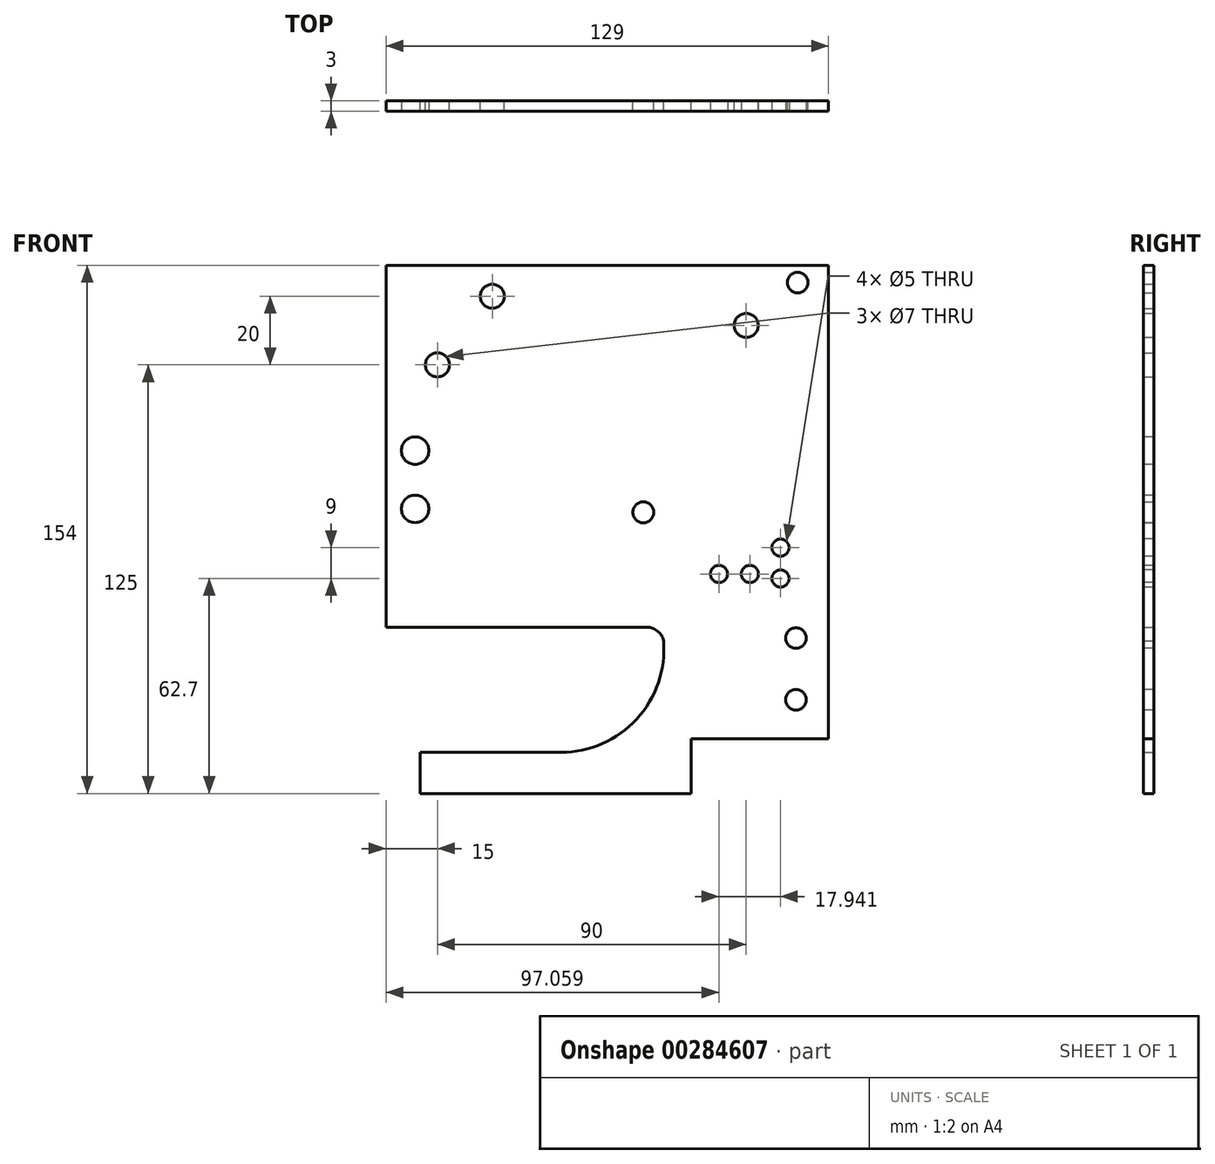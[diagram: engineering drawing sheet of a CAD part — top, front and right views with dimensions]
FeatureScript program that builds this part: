
annotation { "Feature Type Name" : "Feature", "Feature Type Description" : "" }
export const myFeature = defineFeature(function(context is Context, id is Id, definition is map)
    precondition{}
    {
        {
            var Q0;
            Q0=qCreatedBy(makeId("Front.planeOp"),FACE);
            var sketch = newSketch(context, id + "F0", { "sketchPlane" : qUnion([Q0])});
            skLineSegment(sketch, "E0", {"start": v(0, 0) * mm, "end": v(129, 0) * mm});
            skLineSegment(sketch, "E1", {"start": v(129, 0) * mm, "end": v(129, -138) * mm});
            skLineSegment(sketch, "E2", {"start": v(129, -138) * mm, "end": v(89, -138) * mm});
            skLineSegment(sketch, "E3", {"start": v(89, -138) * mm, "end": v(89, -154) * mm});
            skLineSegment(sketch, "E4", {"start": v(89, -154) * mm, "end": v(10, -154) * mm});
            skLineSegment(sketch, "E5", {"start": v(10, -154) * mm, "end": v(10, -142) * mm});
            skLineSegment(sketch, "E6", {"start": v(0, 0) * mm, "end": v(0, -105.5) * mm});
            skLineSegment(sketch, "E7", {"start": v(0, -105.5) * mm, "end": v(76, -105.5) * mm});
            skLineSegment(sketch, "E8", {"start": v(10, -142) * mm, "end": v(51, -142) * mm});
            skLineSegment(sketch, "E9", {"start": v(51, -142) * mm, "end": v(51, -112) * mm, "construction": true});
            skArc(sketch, "E10", {"start": v(51, -142) * mm, "mid": v(73.09, -132.3) * mm, "end": v(80.9, -109.47) * mm});
            skArc(sketch, "E11", {"start": v(80.9, -109.47) * mm, "mid": v(79.15, -106.62) * mm, "end": v(76, -105.5) * mm});
            skLineSegment(sketch, "E12", {"start": v(75, -154) * mm, "end": v(75, -127) * mm, "construction": true});
            skLineSegment(sketch, "E13", {"start": v(75, -127) * mm, "end": v(129, -127) * mm, "construction": true});
            skLineSegment(sketch, "E14", {"start": v(120, -138) * mm, "end": v(120, -99) * mm, "construction": true});
            skLineSegment(sketch, "E15", {"start": v(120, -99) * mm, "end": v(129, -99) * mm, "construction": true});
            skLineSegment(sketch, "E16", {"start": v(120, -99) * mm, "end": v(120, -5) * mm, "construction": true});
            skLineSegment(sketch, "E17", {"start": v(0, -9) * mm, "end": v(31, -9) * mm, "construction": true});
            skLineSegment(sketch, "E18", {"start": v(31, -9) * mm, "end": v(31, 0) * mm, "construction": true});
            skLineSegment(sketch, "E19", {"start": v(0, -29) * mm, "end": v(15, -29) * mm, "construction": true});
            skLineSegment(sketch, "E20", {"start": v(15, -29) * mm, "end": v(15, 0) * mm, "construction": true});
            skLineSegment(sketch, "E21", {"start": v(105, 0) * mm, "end": v(105, -17.5) * mm, "construction": true});
            skLineSegment(sketch, "E22", {"start": v(105, -17.5) * mm, "end": v(129, -17.5) * mm, "construction": true});
            skLineSegment(sketch, "E23", {"start": v(75, -127) * mm, "end": v(75, -72) * mm, "construction": true});
            skSolve(sketch);
        }
        {
            var Q0;
            Q0=qSketchRegion(id+"F0",true);
            extrude(context, id + "F1", {"entities" : qUnion([Q0]), "depth" : 3 * mm});
        }
        {
            var Q0;
            Q0=sQuery(id+"F0.wireOp",VERTEX,"E16.end");
            var Q1;
            Q1=makeQuery(id+"F1.opExtrude","SWEPT_BODY",BODY,{"disambiguationData":[OSD([sQuery(id+"F0.wireOp",EDGE,"E0"),sQuery(id+"F0.wireOp",EDGE,"E1"),sQuery(id+"F0.wireOp",EDGE,"E2"),sQuery(id+"F0.wireOp",EDGE,"E3"),sQuery(id+"F0.wireOp",EDGE,"E4"),sQuery(id+"F0.wireOp",EDGE,"E5"),sQuery(id+"F0.wireOp",EDGE,"E6"),sQuery(id+"F0.wireOp",EDGE,"E7"),sQuery(id+"F0.wireOp",EDGE,"E8"),sQuery(id+"F0.wireOp",EDGE,"E10"),sQuery(id+"F0.wireOp",EDGE,"E11")])]});
            hole(context, id + "F2", {"style" : HoleStyle.SIMPLE, "endStyle" : HoleEndStyle.THROUGH, "oppositeDirection" : true, "holeDiameter" : 6 * mm, "locations" : qUnion([Q0]), "scope" : qUnion([Q1]), "tappedDepth" : 12 * mm, "tapClearance" : 3});
        }
        {
            var Q0;
            Q0=sQuery(id+"F0.wireOp",VERTEX,"E19.end");
            var Q1;
            Q1=sQuery(id+"F0.wireOp",VERTEX,"E18.start");
            var Q2;
            Q2=sQuery(id+"F0.wireOp",VERTEX,"E21.end");
            var Q3;
            Q3=makeQuery(id+"F1.opExtrude","SWEPT_BODY",BODY,{"disambiguationData":[OSD([sQuery(id+"F0.wireOp",EDGE,"E0"),sQuery(id+"F0.wireOp",EDGE,"E1"),sQuery(id+"F0.wireOp",EDGE,"E2"),sQuery(id+"F0.wireOp",EDGE,"E3"),sQuery(id+"F0.wireOp",EDGE,"E4"),sQuery(id+"F0.wireOp",EDGE,"E5"),sQuery(id+"F0.wireOp",EDGE,"E6"),sQuery(id+"F0.wireOp",EDGE,"E7"),sQuery(id+"F0.wireOp",EDGE,"E8"),sQuery(id+"F0.wireOp",EDGE,"E10"),sQuery(id+"F0.wireOp",EDGE,"E11")])]});
            hole(context, id + "F3", {"style" : HoleStyle.SIMPLE, "endStyle" : HoleEndStyle.THROUGH, "oppositeDirection" : true, "holeDiameter" : 7 * mm, "locations" : qUnion([Q0, Q1, Q2]), "scope" : qUnion([Q3]), "isTappedThrough" : true});
        }
        {
            var Q0;
            Q0=sQuery(id+"F0.wireOp",VERTEX,"E23.end");
            var Q1;
            Q1=makeQuery(id+"F1.opExtrude","SWEPT_BODY",BODY,{"disambiguationData":[OSD([sQuery(id+"F0.wireOp",EDGE,"E0"),sQuery(id+"F0.wireOp",EDGE,"E1"),sQuery(id+"F0.wireOp",EDGE,"E2"),sQuery(id+"F0.wireOp",EDGE,"E3"),sQuery(id+"F0.wireOp",EDGE,"E4"),sQuery(id+"F0.wireOp",EDGE,"E5"),sQuery(id+"F0.wireOp",EDGE,"E6"),sQuery(id+"F0.wireOp",EDGE,"E7"),sQuery(id+"F0.wireOp",EDGE,"E8"),sQuery(id+"F0.wireOp",EDGE,"E10"),sQuery(id+"F0.wireOp",EDGE,"E11")])]});
            hole(context, id + "F4", {"style" : HoleStyle.SIMPLE, "endStyle" : HoleEndStyle.THROUGH, "oppositeDirection" : true, "holeDiameter" : 6.1 * mm, "locations" : qUnion([Q0]), "scope" : qUnion([Q1]), "isTappedThrough" : true});
        }
        {
            var Q0;
            Q0=makeQuery(id+"F1.opExtrude","CAP_FACE",FACE,{"disambiguationData":[OSD([sQuery(id+"F0.wireOp",EDGE,"E0"),sQuery(id+"F0.wireOp",EDGE,"E1"),sQuery(id+"F0.wireOp",EDGE,"E2"),sQuery(id+"F0.wireOp",EDGE,"E3"),sQuery(id+"F0.wireOp",EDGE,"E4"),sQuery(id+"F0.wireOp",EDGE,"E5"),sQuery(id+"F0.wireOp",EDGE,"E6"),sQuery(id+"F0.wireOp",EDGE,"E7"),sQuery(id+"F0.wireOp",EDGE,"E8"),sQuery(id+"F0.wireOp",EDGE,"E10"),sQuery(id+"F0.wireOp",EDGE,"E11")])],"isStart":false});
            var sketch = newSketch(context, id + "F5", { "sketchPlane" : qUnion([Q0])});
            skLineSegment(sketch, "E24", {"start": v(97.06, 0) * mm, "end": v(97.06, -89.97) * mm, "construction": true});
            skLineSegment(sketch, "E25", {"start": v(97.06, -89.97) * mm, "end": v(129, -89.97) * mm, "construction": true});
            skPoint(sketch, "E26", {"position": v(106.06, -89.97) * mm});
            skLineSegment(sketch, "E27", {"start": v(115, 0) * mm, "end": v(115, -82.3) * mm, "construction": true});
            skLineSegment(sketch, "E28", {"start": v(115, -82.3) * mm, "end": v(129, -82.3) * mm, "construction": true});
            skPoint(sketch, "E29", {"position": v(115, -91.3) * mm});
            skLineSegment(sketch, "E30", {"start": v(8.5, -154) * mm, "end": v(8.5, -54) * mm, "construction": true});
            skLineSegment(sketch, "E31", {"start": v(8.5, -54) * mm, "end": v(0, -54) * mm, "construction": true});
            skPoint(sketch, "E32", {"position": v(8.5, -71) * mm});
            skLineSegment(sketch, "E33", {"start": v(119.5, -138) * mm, "end": v(119.5, -108.67) * mm, "construction": true});
            skLineSegment(sketch, "E34", {"start": v(119.5, -108.67) * mm, "end": v(129, -108.67) * mm, "construction": true});
            skPoint(sketch, "E35", {"position": v(119.5, -126.67) * mm});
            skSolve(sketch);
        }
        {
            var Q0;
            Q0=sQuery(id+"F5.wireOp",VERTEX,"E26");
            var Q1;
            Q1=sQuery(id+"F5.wireOp",VERTEX,"E29");
            var Q2;
            Q2=sQuery(id+"F5.wireOp",VERTEX,"E28.start");
            var Q3;
            Q3=sQuery(id+"F5.wireOp",VERTEX,"E25.start");
            var Q4;
            Q4=makeQuery(id+"F1.opExtrude","SWEPT_BODY",BODY,{"disambiguationData":[OSD([sQuery(id+"F0.wireOp",EDGE,"E0"),sQuery(id+"F0.wireOp",EDGE,"E1"),sQuery(id+"F0.wireOp",EDGE,"E2"),sQuery(id+"F0.wireOp",EDGE,"E3"),sQuery(id+"F0.wireOp",EDGE,"E4"),sQuery(id+"F0.wireOp",EDGE,"E5"),sQuery(id+"F0.wireOp",EDGE,"E6"),sQuery(id+"F0.wireOp",EDGE,"E7"),sQuery(id+"F0.wireOp",EDGE,"E8"),sQuery(id+"F0.wireOp",EDGE,"E10"),sQuery(id+"F0.wireOp",EDGE,"E11")])]});
            hole(context, id + "F6", {"style" : HoleStyle.SIMPLE, "endStyle" : HoleEndStyle.THROUGH, "holeDiameter" : 5 * mm, "locations" : qUnion([Q0, Q1, Q2, Q3]), "scope" : qUnion([Q4]), "isTappedThrough" : true});
        }
        {
            var Q0;
            Q0=sQuery(id+"F5.wireOp",VERTEX,"E32");
            var Q1;
            Q1=sQuery(id+"F5.wireOp",VERTEX,"E31.start");
            var Q2;
            Q2=makeQuery(id+"F1.opExtrude","SWEPT_BODY",BODY,{"disambiguationData":[OSD([sQuery(id+"F0.wireOp",EDGE,"E0"),sQuery(id+"F0.wireOp",EDGE,"E1"),sQuery(id+"F0.wireOp",EDGE,"E2"),sQuery(id+"F0.wireOp",EDGE,"E3"),sQuery(id+"F0.wireOp",EDGE,"E4"),sQuery(id+"F0.wireOp",EDGE,"E5"),sQuery(id+"F0.wireOp",EDGE,"E6"),sQuery(id+"F0.wireOp",EDGE,"E7"),sQuery(id+"F0.wireOp",EDGE,"E8"),sQuery(id+"F0.wireOp",EDGE,"E10"),sQuery(id+"F0.wireOp",EDGE,"E11")])]});
            hole(context, id + "F7", {"style" : HoleStyle.SIMPLE, "endStyle" : HoleEndStyle.THROUGH, "holeDiameter" : 8 * mm, "locations" : qUnion([Q0, Q1]), "scope" : qUnion([Q2]), "isTappedThrough" : true});
        }
        {
            var Q0;
            Q0=sQuery(id+"F5.wireOp",VERTEX,"E34.start");
            var Q1;
            Q1=sQuery(id+"F5.wireOp",VERTEX,"E35");
            var Q2;
            Q2=makeQuery(id+"F1.opExtrude","SWEPT_BODY",BODY,{"disambiguationData":[OSD([sQuery(id+"F0.wireOp",EDGE,"E0"),sQuery(id+"F0.wireOp",EDGE,"E1"),sQuery(id+"F0.wireOp",EDGE,"E2"),sQuery(id+"F0.wireOp",EDGE,"E3"),sQuery(id+"F0.wireOp",EDGE,"E4"),sQuery(id+"F0.wireOp",EDGE,"E5"),sQuery(id+"F0.wireOp",EDGE,"E6"),sQuery(id+"F0.wireOp",EDGE,"E7"),sQuery(id+"F0.wireOp",EDGE,"E8"),sQuery(id+"F0.wireOp",EDGE,"E10"),sQuery(id+"F0.wireOp",EDGE,"E11")])]});
            hole(context, id + "F8", {"style" : HoleStyle.SIMPLE, "endStyle" : HoleEndStyle.THROUGH, "holeDiameter" : 6 * mm, "locations" : qUnion([Q0, Q1]), "scope" : qUnion([Q2]), "isTappedThrough" : true});
        }
    });
